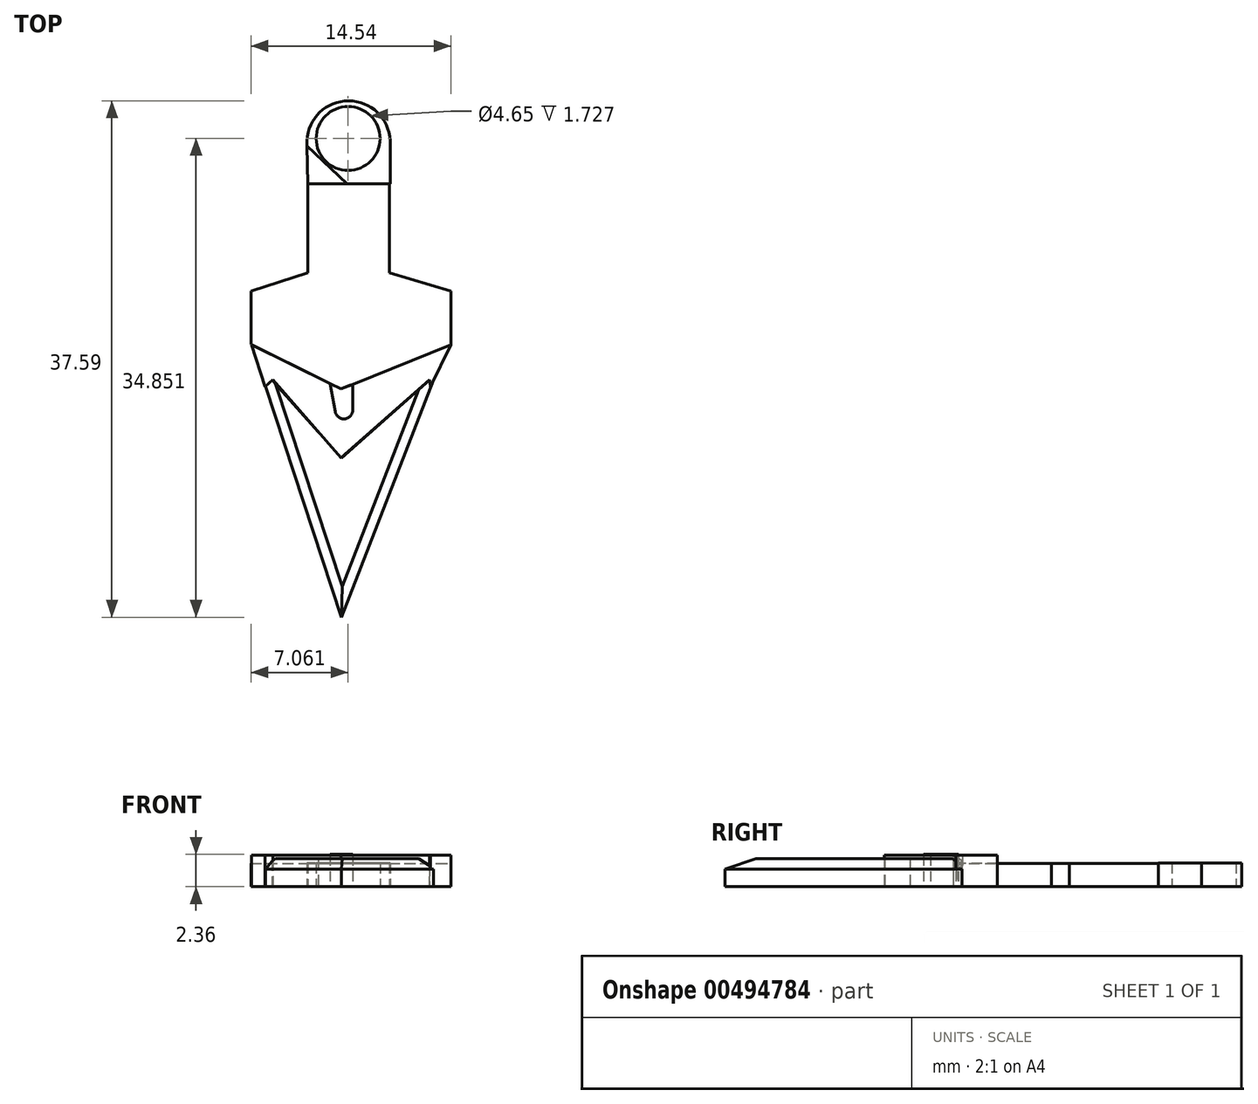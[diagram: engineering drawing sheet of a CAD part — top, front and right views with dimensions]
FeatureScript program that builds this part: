
annotation { "Feature Type Name" : "Feature", "Feature Type Description" : "" }
export const myFeature = defineFeature(function(context is Context, id is Id, definition is map)
    precondition{}
    {
        {
            var Q0;
            Q0=qCreatedBy(makeId("Top.planeOp"),FACE);
            var sketch = newSketch(context, id + "F0", { "sketchPlane" : qUnion([Q0])});
            skLineSegment(sketch, "E0", {"start": v(-76.08, -6.72) * mm, "end": v(-69.23, 10.94) * mm});
            skLineSegment(sketch, "E1", {"start": v(-69.23, 10.94) * mm, "end": v(-76.08, 4.87) * mm});
            skLineSegment(sketch, "E2", {"start": v(-76.08, 4.87) * mm, "end": v(-82.14, 11.7) * mm});
            skLineSegment(sketch, "E3", {"start": v(-82.14, 11.7) * mm, "end": v(-76.08, -6.72) * mm});
            skSolve(sketch);
        }
        {
            var Q0;
            Q0=qSketchRegion(id+"F0",true);
            extrude(context, id + "F1", {"entities" : qUnion([Q0]), "depth" : 2.03 * mm});
        }
        {
            var Q0;
            Q0=makeQuery(id+"F1.opExtrude","CAP_EDGE",EDGE,{"disambiguationData":[OSD([sQuery(id+"F0.wireOp",EDGE,"E3")])],"isStart":false});
            var Q1;
            Q1=makeQuery(id+"F1.opExtrude","CAP_EDGE",EDGE,{"disambiguationData":[OSD([sQuery(id+"F0.wireOp",EDGE,"E0")])],"isStart":false});
            chamfer(context, id + "F2", {"entities" : qUnion([Q0, Q1]), "chamferType" : ChamferType.OFFSET_ANGLE, "width" : 0.76 * mm, "oppositeDirection" : false, "angle" : 45 * degree, "tangentPropagation" : true});
        }
        {
            var Q0;
            Q0=makeQuery(id+"F1.opExtrude","SWEPT_BODY",BODY,{"disambiguationData":[OSD([sQuery(id+"F0.wireOp",EDGE,"E0"),sQuery(id+"F0.wireOp",EDGE,"E1"),sQuery(id+"F0.wireOp",EDGE,"E2"),sQuery(id+"F0.wireOp",EDGE,"E3")])]});
            var Q1;
            Q1=qCreatedBy(makeId("Right.planeOp"),FACE);
            transform(context, id + "F3", {"entities" : qUnion([Q0]), "transformType" : TransformType.TRANSLATION_DISTANCE, "transformDirection" : qUnion([Q1]), "distance" : 62.74 * mm, "makeCopy" : false});
        }
        {
            var Q0;
            Q0=qCreatedBy(makeId("Top.planeOp"),FACE);
            var sketch = newSketch(context, id + "F4", { "sketchPlane" : qUnion([Q0])});
            skLineSegment(sketch, "E4", {"start": v(-13.39, 4.88) * mm, "end": v(-18.34, 10.57) * mm});
            skLineSegment(sketch, "E5", {"start": v(-18.34, 10.57) * mm, "end": v(-18.9, 10.08) * mm});
            skLineSegment(sketch, "E6", {"start": v(-18.9, 10.08) * mm, "end": v(-19.9, 13.1) * mm});
            skLineSegment(sketch, "E7", {"start": v(-19.9, 13.1) * mm, "end": v(-13.39, 9.9) * mm});
            skLineSegment(sketch, "E8", {"start": v(-6.92, 10.57) * mm, "end": v(-6.87, 10.08) * mm});
            skLineSegment(sketch, "E9", {"start": v(-6.87, 10.08) * mm, "end": v(-5.38, 13.1) * mm});
            skLineSegment(sketch, "E10", {"start": v(-5.38, 13.1) * mm, "end": v(-13.39, 9.9) * mm});
            skLineSegment(sketch, "E11", {"start": v(-14.17, 10.28) * mm, "end": v(-13.8, 8.24) * mm});
            skLineSegment(sketch, "E12", {"start": v(-12.54, 8.24) * mm, "end": v(-12.54, 10.28) * mm});
            skArc(sketch, "E13", {"start": v(-13.8, 8.24) * mm, "mid": v(-13.17, 7.72) * mm, "end": v(-12.54, 8.24) * mm});
            skLineSegment(sketch, "E14", {"start": v(-13.39, 4.88) * mm, "end": v(-6.92, 10.57) * mm});
            skSolve(sketch);
        }
        {
            var Q0;
            Q0=qSketchRegion(id+"F4",true);
            extrude(context, id + "F5", {"entities" : qUnion([Q0]), "operationType" : NewBodyOperationType.ADD, "depth" : 2.3 * mm});
        }
        {
            var Q0;
            {var subQ6=sQuery(id+"F4.wireOp",EDGE,"E11");Q0=makeQuery(id+"F4.imprint","IMPRINT",FACE,{"disambiguationData":[TD([[makeQuery(id+"F4.imprint","IMPRINT",EDGE,{"derivedFrom":subQ6}),1.0]])]});}
            var Q1;
            Q1=sQuery(id+"F4.wireOp",EDGE,"E11");
            var Q2;
            Q2=sQuery(id+"F4.wireOp",EDGE,"E13");
            var Q3;
            Q3=sQuery(id+"F4.wireOp",EDGE,"E12");
            var Q4;
            Q4=sQuery(id+"F4.wireOp",EDGE,"E10");
            var Q5;
            Q5=sQuery(id+"F4.wireOp",EDGE,"E7");
            extrude(context, id + "F6", {"entities" : qUnion([Q0]), "surfaceEntities" : qUnion([Q1, Q2, Q3, Q4, Q5]), "depth" : 2.36 * mm});
        }
        {
            var Q0;
            Q0=qCreatedBy(makeId("Top.planeOp"),FACE);
            var sketch = newSketch(context, id + "F7", { "sketchPlane" : qUnion([Q0])});
            skLineSegment(sketch, "E15.MirrorCS", {"start": v(-5.38, 13.1) * mm, "end": v(-5.38, 17.03) * mm});
            skLineSegment(sketch, "E16", {"start": v(-19.92, 13.13) * mm, "end": v(-13.4, 9.9) * mm});
            skLineSegment(sketch, "E17", {"start": v(-13.4, 9.9) * mm, "end": v(-5.38, 13.1) * mm});
            skLineSegment(sketch, "E18", {"start": v(-19.92, 13.13) * mm, "end": v(-19.92, 17.03) * mm});
            skLineSegment(sketch, "E19", {"start": v(-19.92, 17.03) * mm, "end": v(-15.79, 18.35) * mm});
            skLineSegment(sketch, "E20", {"start": v(-15.79, 18.35) * mm, "end": v(-15.79, 24.82) * mm});
            skLineSegment(sketch, "E21", {"start": v(-15.79, 24.82) * mm, "end": v(-9.84, 24.82) * mm});
            skLineSegment(sketch, "E22", {"start": v(-9.84, 24.82) * mm, "end": v(-9.84, 18.35) * mm});
            skLineSegment(sketch, "E23", {"start": v(-9.84, 18.35) * mm, "end": v(-5.38, 17.03) * mm});
            skSolve(sketch);
        }
        {
            var Q0;
            Q0=qSketchRegion(id+"F7",true);
            extrude(context, id + "F8", {"entities" : qUnion([Q0]), "depth" : 1.7 * mm});
        }
        {
            var Q0;
            Q0=qCreatedBy(makeId("Top.planeOp"),FACE);
            var sketch = newSketch(context, id + "F9", { "sketchPlane" : qUnion([Q0])});
            skCircle(sketch, "E24", {"center": v(-12.83, 27.85) * mm, "radius": 3.02 * mm});
            skLineSegment(sketch, "E25", {"start": v(-15.79, 24.82) * mm, "end": v(-12.9, 24.82) * mm, "construction": true});
            skLineSegment(sketch, "E26", {"start": v(-15.79, 24.82) * mm, "end": v(-15.85, 27.97) * mm});
            skLineSegment(sketch, "E27", {"start": v(-9.8, 27.97) * mm, "end": v(-9.8, 24.82) * mm});
            skPoint(sketch, "E27.endSnap0", {"position": v(-14.34, 24.82) * mm});
            skLineSegment(sketch, "E28", {"start": v(-9.8, 24.82) * mm, "end": v(-12.9, 24.82) * mm});
            skSolve(sketch);
        }
        {
            var Q0;
            {var subQ0=sQuery(id+"F9.wireOp",EDGE,"E26");var subQ1=sQuery(id+"F9.wireOp",EDGE,"E24");var subQ2=makeQuery(id+"F9.imprint","INTERSECT",VERTEX,{"disambiguationData":[OD(0.0)],"derivedFrom":[subQ1,subQ0]});Q0=makeQuery(id+"F9.imprint","IMPRINT",FACE,{"disambiguationData":[TD([[makeQuery(id+"F9.imprint","IMPRINT",EDGE,{"disambiguationData":[TD([[subQ2,1.0]])],"derivedFrom":subQ1}),1.0]])]});}
            var Q1;
            {var subQ0=sQuery(id+"F9.wireOp",EDGE,"E28");var subQ1=sQuery(id+"F9.wireOp",EDGE,"E24");var subQ2=makeQuery(id+"F9.imprint","INTERSECT",VERTEX,{"disambiguationData":[OD(1.0)],"derivedFrom":[subQ1,subQ0]});Q1=makeQuery(id+"F9.imprint","IMPRINT",FACE,{"disambiguationData":[TD([[makeQuery(id+"F9.imprint","IMPRINT",EDGE,{"disambiguationData":[TD([[subQ2,-1.0]])],"derivedFrom":subQ1}),-1.0]])]});}
            extrude(context, id + "F10", {"entities" : qUnion([Q0, Q1]), "operationType" : NewBodyOperationType.ADD, "depth" : 1.73 * mm});
        }
        {
            var Q0;
            Q0=qCreatedBy(makeId("Top.planeOp"),FACE);
            var sketch = newSketch(context, id + "F11", { "sketchPlane" : qUnion([Q0])});
            skCircle(sketch, "E29", {"center": v(-12.86, 28.13) * mm, "radius": 2.33 * mm});
            skSolve(sketch);
        }
        {
            var Q0;
            Q0=qSketchRegion(id+"F11",true);
            extrude(context, id + "F12", {"entities" : qUnion([Q0]), "operationType" : NewBodyOperationType.REMOVE, "depth" : 6.6 * mm});
        }
        {
            var Q0;
            Q0=qCreatedBy(makeId("Top.planeOp"),FACE);
            var sketch = newSketch(context, id + "F13", { "sketchPlane" : qUnion([Q0])});
            skLineSegment(sketch, "E30", {"start": v(-15.84, 27.6) * mm, "end": v(-15.79, 24.82) * mm});
            skLineSegment(sketch, "E31", {"start": v(-15.79, 24.82) * mm, "end": v(-12.95, 24.82) * mm});
            skLineSegment(sketch, "E32", {"start": v(-12.95, 24.82) * mm, "end": v(-15.84, 27.6) * mm});
            skSolve(sketch);
        }
        {
            var Q0;
            Q0=qSketchRegion(id+"F13",true);
            extrude(context, id + "F14", {"entities" : qUnion([Q0]), "operationType" : NewBodyOperationType.ADD, "depth" : 1.73 * mm});
        }
    });
